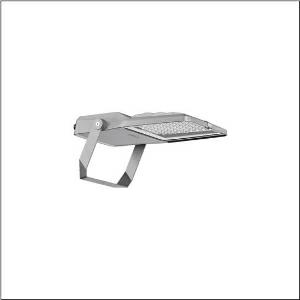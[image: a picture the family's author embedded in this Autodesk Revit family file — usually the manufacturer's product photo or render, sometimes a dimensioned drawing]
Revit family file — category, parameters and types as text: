
# Revit family: floodlight_fl_21_mini___pl61_5xa7772c2c1a_b005
name_source: partatom
category: Lighting Fixtures
units: mm (PartAtom-declared; Revit-internal decimal feet)

## family parameters
Cut with Voids When Loaded = No
Host = Face
Light Source = No
Part Type = Normal
Room Calculation Point = No
Round Connector Dimension = Use Diameter
Shared = No

## types (1)
- --- (1 x LED, 11980 lm, 87.2 W, 3000K)
    Apparent Load = 87 VA
    CIE Flux Codes = 33 65 98 100 100
    Color Rendering = 70
    Color Temperature = 3000K
    Default Elevation = 1800 mm
    Description = Floodlight FL 21 mini, floodlight, primary light control with lens, of PMMA, primary optical cover: protective disc, of toughened safety glass, transparent, light distribution: PL61, light emission: direct distribution, installation type: surface-mounted, LED, High Power LED, rated luminous flux: 11.980lm, luminous efficacy: 137lm/W, light colour: 730, colour temperature: 3000K, control gear: ECG iQ, control: Street-Remote, Auto-Match, Temp-Guard, Night-Set, Smart-Wire, Desk-Remote (wireless, voltage-free reading and setting of iQ features in the workshop via application-optimized NFC function/RFID function), optimised constant luminous flux control (CLO 2.0), with terminal, 6-pole, mains connection: 220..240V, AC, 50/60Hz, start of lifetime: 87W, end of lifetime: 92W, reduction: 40W, luminaire housing, of diecast aluminium, powder-coated, Siteco® metallic grey (DB 702S), corrosivity category C5 according to DIN EN ISO 12944, mounting bracket, of steel, galvanised, powder-coated, Siteco® metallic grey (DB 702S), protection rating (complete): IP66, insulation class (complete): insulation class II (safety insulation), certification: CE, ENEC, VDE, protection symbol: D, impact resistance: IK08, permissible operating ambient temperature: -40..+40°C, permissible operating ambient temperature for outdoor applications: -40..+50°C, standard: DIN EN 12944, packaging unit: 1 piece

Light Distribution: PL61
    Height = 70 mm
    Lamp = 1 x LED
    Lamp Light Flux = 11980 lm
    Lamp Power = 87.2 W
    Lamp count = 1
    Length = 485 mm
    Luminous efficacy = 137 lm/W
    Manufacturer = Siteco
    ModVariant = No
    Model = 5XA7772C2C1A
    Number of Poles = 1
    OnlyDefault = Yes
    Power Factor = 1
    Product Name = Floodlight FL 21 mini | PL61
    Product group = floodlight | pylon top
    ProductGroupID = 6101
    Protection Class = Protection class II
    Protection Degree = IP 66
    RLX_Detail_Level = 1
    RlxData = <blob elided: 96173 chars, md5=f26925f7>
    Socket = socket
    Standby Power = 0 W
    System Light Flux = 11980 lm
    System Power = 87 W
    Type Comments = factory setting: luminous flux: 100 % | dim-lin: 254 | 456 mA
    Type Image = l_1006845.jpg
    URL = http://relux.com
    VarID = @adj_085441
    Voltage = 0 V
    Weight = 0.00 kg
    Width = 337 mm

## geometry (parser evidence)
native form markers: Blend x4, Sweep x13
no freeform markers — native parametric forms only
